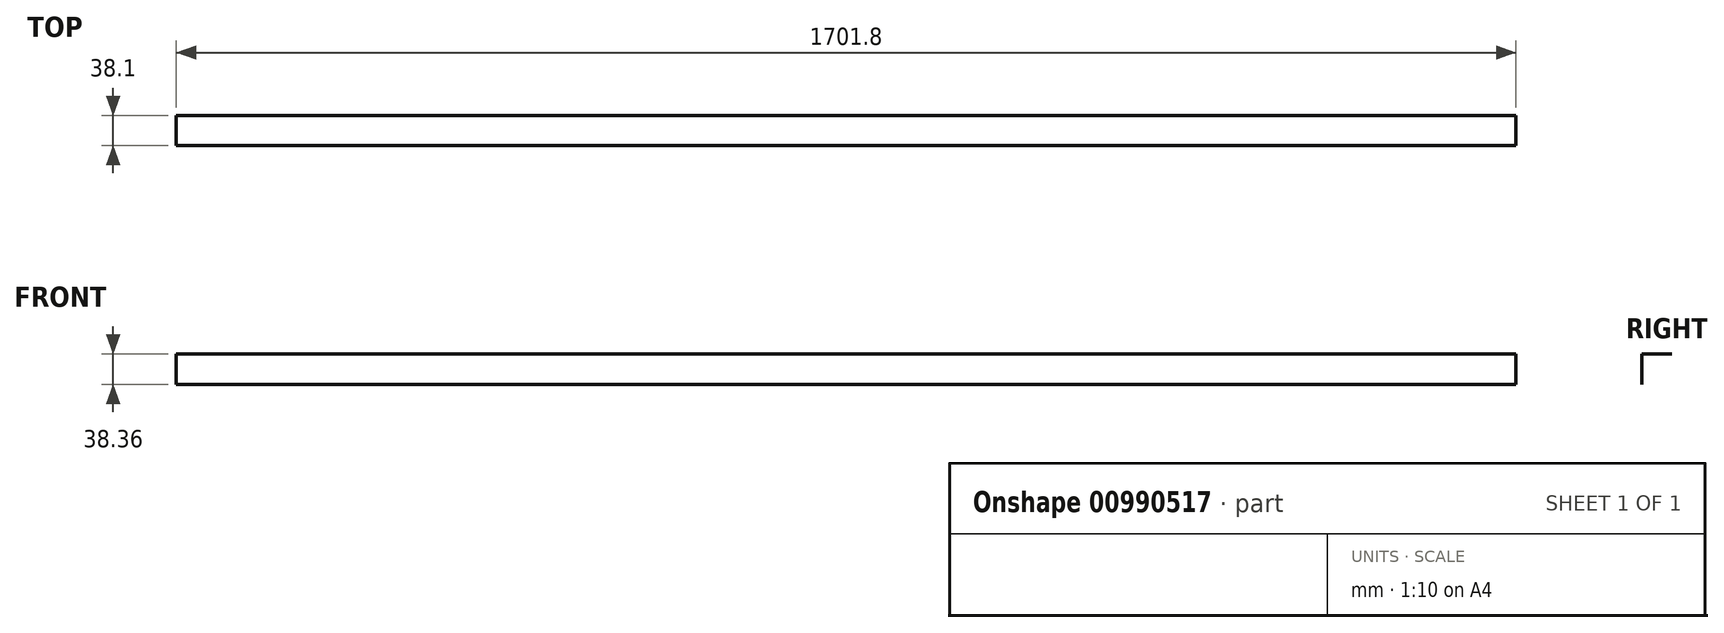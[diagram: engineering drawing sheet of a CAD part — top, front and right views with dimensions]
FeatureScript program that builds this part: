
annotation { "Feature Type Name" : "Feature", "Feature Type Description" : "" }
export const myFeature = defineFeature(function(context is Context, id is Id, definition is map)
    precondition{}
    {
        {
            var Q0;
            Q0=qCreatedBy(makeId("Right.planeOp"),FACE);
            var sketch = newSketch(context, id + "F0", { "sketchPlane" : qUnion([Q0])});
            skLineSegment(sketch, "E0", {"start": v(-9.4, 30.6) * mm, "end": v(-9.4, -7.75) * mm});
            skLineSegment(sketch, "E1", {"start": v(-9.4, 30.6) * mm, "end": v(28.7, 30.6) * mm});
            skSolve(sketch);
        }
        {
            var Q0;
            Q0=sQuery(id+"F0.wireOp",EDGE,"E1");
            var Q1;
            Q1=sQuery(id+"F0.wireOp",EDGE,"E0");
            extrude(context, id + "F1", {"bodyType" : ToolBodyType.SURFACE, "operationType" : NewBodyOperationType.ADD, "surfaceEntities" : qUnion([Q0, Q1]), "depth" : 1701.8 * mm, "offsetDistance" : 25.4 * mm});
        }
    });
